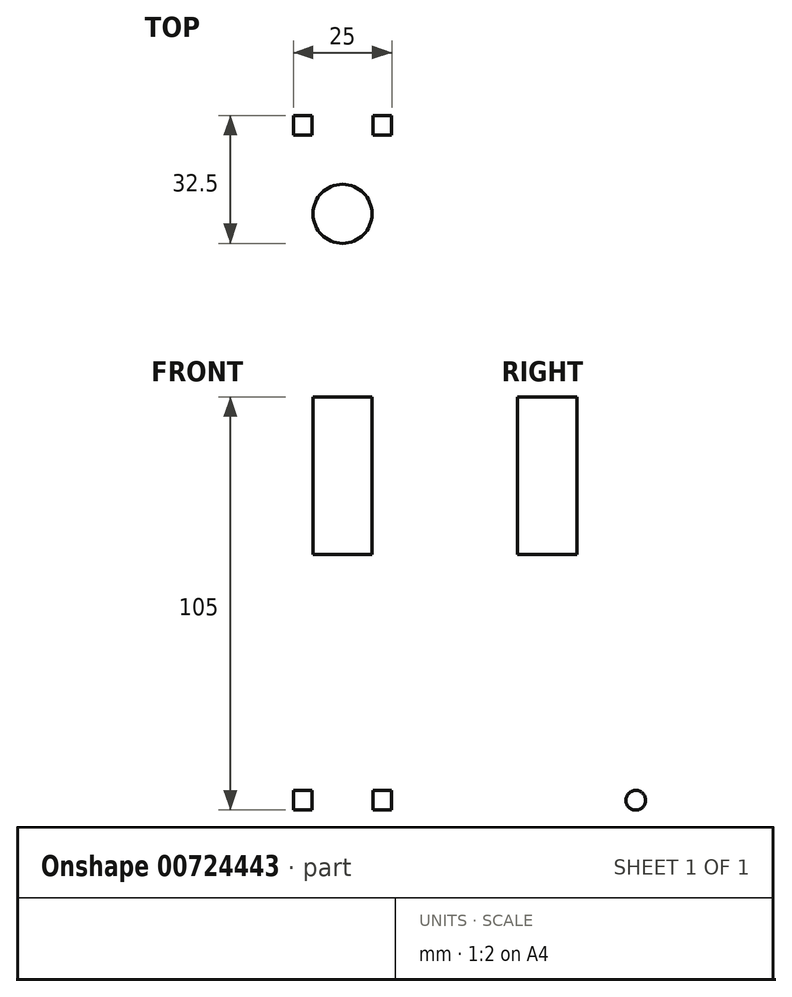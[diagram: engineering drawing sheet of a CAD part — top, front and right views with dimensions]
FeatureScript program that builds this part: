
annotation { "Feature Type Name" : "Feature", "Feature Type Description" : "" }
export const myFeature = defineFeature(function(context is Context, id is Id, definition is map)
    precondition{}
    {
        {
            var Q0;
            Q0=qCreatedBy(makeId("Front.planeOp"),FACE);
            var sketch = newSketch(context, id + "F0", { "sketchPlane" : qUnion([Q0])});
            skLineSegment(sketch, "E0.bottom", {"start": v(-11.08, 60.02) * mm, "end": v(13.92, 60.02) * mm});
            skLineSegment(sketch, "E0.top", {"start": v(-11.08, -19.98) * mm, "end": v(13.92, -19.98) * mm});
            skLineSegment(sketch, "E0.left", {"start": v(-11.08, 60.02) * mm, "end": v(-11.08, -19.98) * mm});
            skLineSegment(sketch, "E0.right", {"start": v(13.92, 60.02) * mm, "end": v(13.92, -19.98) * mm});
            skLineSegment(sketch, "E1.bottom", {"start": v(-6.38, -19.98) * mm, "end": v(9.22, -19.98) * mm});
            skLineSegment(sketch, "E1.top", {"start": v(-6.38, 40.02) * mm, "end": v(9.22, 40.02) * mm});
            skLineSegment(sketch, "E1.left", {"start": v(-6.38, -19.98) * mm, "end": v(-6.38, 40.02) * mm});
            skLineSegment(sketch, "E1.right", {"start": v(9.22, -19.98) * mm, "end": v(9.22, 40.02) * mm});
            skSolve(sketch);
        }
        {
            var Q0;
            Q0=makeQuery(id+"F0.imprint","IMPRINT",FACE,{"disambiguationData":[TD([[makeQuery(id+"F0.imprint","IMPRINT",EDGE,{"derivedFrom":sQuery(id+"F0.wireOp",EDGE,"E0.bottom")}),-1.0]])]});
            extrude(context, id + "F1", {"entities" : qUnion([Q0]), "depth" : 80 * mm, "offsetDistance" : 25 * mm});
        }
        {
            var Q0;
            Q0=makeQuery(id+"F1.opExtrude","SWEPT_FACE",FACE,{"disambiguationData":[OSD([sQuery(id+"F0.wireOp",EDGE,"E0.bottom")])]});
            var sketch = newSketch(context, id + "F2", { "sketchPlane" : qUnion([Q0])});
            skCircle(sketch, "E2", {"center": v(1.42, -40) * mm, "radius": 7.5 * mm});
            skSolve(sketch);
        }
        {
            var Q0;
            Q0=makeQuery(id+"F2.imprint","IMPRINT",FACE,{"disambiguationData":[TD([[makeQuery(id+"F2.imprint","IMPRINT",EDGE,{"derivedFrom":sQuery(id+"F2.wireOp",EDGE,"E2")}),1.0]])]});
            extrude(context, id + "F3", {"entities" : qUnion([Q0]), "operationType" : NewBodyOperationType.ADD, "depth" : 40 * mm, "offsetDistance" : 25 * mm});
        }
        {
            var Q0;
            Q0=makeQuery(id+"F1.opExtrude","SWEPT_FACE",FACE,{"disambiguationData":[OSD([sQuery(id+"F0.wireOp",EDGE,"E0.right")])]});
            var sketch = newSketch(context, id + "F4", { "sketchPlane" : qUnion([Q0])});
            skCircle(sketch, "E3", {"center": v(-62.5, -2.48) * mm, "radius": 2.5 * mm});
            skCircle(sketch, "E4.MirrorC", {"center": v(-17.5, -2.48) * mm, "radius": 2.5 * mm});
            skSolve(sketch);
        }
        {
            var Q0;
            Q0=makeQuery(id+"F4.imprint","IMPRINT",FACE,{"disambiguationData":[TD([[makeQuery(id+"F4.imprint","IMPRINT",EDGE,{"derivedFrom":sQuery(id+"F4.wireOp",EDGE,"E3")}),1.0]])]});
            var Q1;
            Q1=makeQuery(id+"F4.imprint","IMPRINT",FACE,{"disambiguationData":[TD([[makeQuery(id+"F4.imprint","IMPRINT",EDGE,{"derivedFrom":sQuery(id+"F4.wireOp",EDGE,"E4.MirrorC")}),-1.0]])]});
            extrude(context, id + "F5", {"entities" : qUnion([Q0, Q1]), "operationType" : NewBodyOperationType.REMOVE, "oppositeDirection" : true, "depth" : 50 * mm, "offsetDistance" : 25 * mm});
        }
    });
